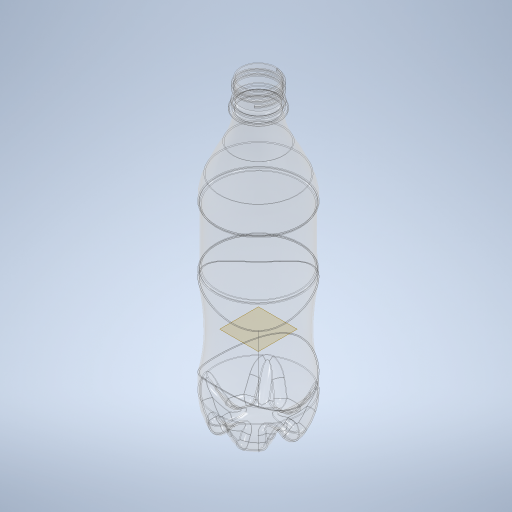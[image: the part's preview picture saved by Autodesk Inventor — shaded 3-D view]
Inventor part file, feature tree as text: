
AUTODESK INVENTOR PART (.ipt)
format: ipt  version: 2024 (Build 280153000, 153)  size: 1,614,336 bytes
history: native  units: mm
features: sketch x10, plane x5, other x3, revolve x2, extrude x2, sweep x2, fillet x2, loft x1, pattern_circular x1, shell x1
ambient origin geometry x8: Origin, YZ Plane, XZ Plane, XY Plane, X Axis, Y Axis, Z Axis, Center Point
bodies: Solid1 (feature_tree)
feature tree (29):
  sketch  "Sketch1"  dims[d0=215.0mm d1=15.0mm]
  revolve  "Revolution1"  [1 undecoded]
  extrude  "Extrusion1"  Depth=5.0mm
  plane  "Work Plane1"
  extrude  "Extrusion2"  Depth=40.0mm
  plane  "Work Plane2"
  loft  "Loft1"
  sketch  "Sketch6"  dims[d10=30.5mm d11=40.0mm d12=1.0mm d13=40.0mm d14=1.0mm d15=75.0mm]
  plane  "Work Plane3"
  sweep  "Sweep1"
  fillet  "Fillet1"  Radius=1.0mm
  pattern_circular  "Circular Pattern1"  Count=4  [1 undecoded]
  fillet  "Fillet2"  Radius=1.0mm
  shell  "Shell1"  Thickness=75.0mm
  revolve  "Revolution2"  [1 undecoded]
  plane  "Work Plane4"
  sketch  "3D Sketch1"
  plane  "Work Plane5"
  sweep  "Sweep2"
  sketch  "Sketch3"  dims[d4=0.5mm d5=5.0mm]
  sketch  "Sketch4"  dims[d6=18.0mm d7=40.0mm]
  sketch  "Sketch5"  dims[d8=27.5mm d9=200.0mm]
  other  "Edges1"
  other  "Edges2"
  sketch  "Sketch7"  dims[d16=7.5mm d17=40.0mm]
  sketch  "Sketch8"  dims[d18=6.0mm d19=25.0mm]
  sketch  "Sketch9"  dims[d24=12.5mm]
  other  "Helical Curve1"
  sketch  "Sketch10"  dims[d25=90.0deg d26=65.0mm d27=90.0mm d28=25.0mm d29=0.0mm d30=0.0mm d31=45.0deg d32=90.0mm d33=15.0mm d34=0.0mm d35=0.0mm d36=-155.0mm d37=55.0mm d38=0.0mm d39=90.0deg d40=0.0mm d41=90.0deg d42=0.0mm d43=90.0deg d44=20.0mm d45=21.380283mm d46=6.0mm d47=2.8mm d48=20.0mm d49=22.5deg d50=22.5deg d51=36.0mm d52=0.0mm d53=0.0mm d54=0.0mm d55=5.0mm d56=50.0mm d57=360.0deg d59=1.0mm d60=0.75mm d61=7.75mm d62=2.25mm d63=2.0mm d64=1.745329mm d65=1.0mm d66=0.5mm d67=0.5mm d68=1.0mm d69=1.7mm d70=90.0deg d71=-2.0mm d72=3.0mm d73=24.0mm d74=25.0mm d75=0.0mm d76=1.5mm d77=1.15mm d78=30.0deg d79=0.0mm d80=0.0mm]
note: 3 required parameter values undecoded (feature->parameter linkage not recoverable at this tier; creation-order binding heuristic only, values carry confidence <= 0.55)